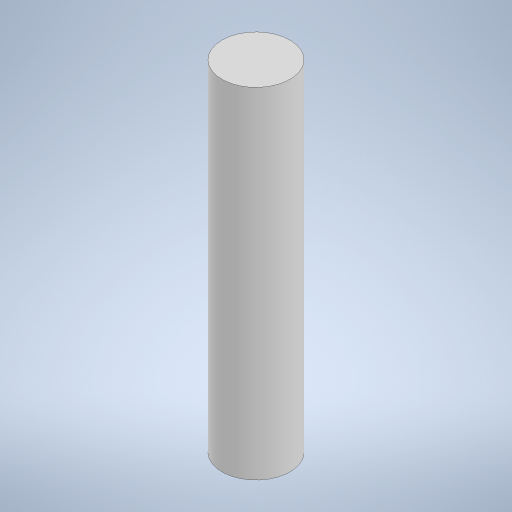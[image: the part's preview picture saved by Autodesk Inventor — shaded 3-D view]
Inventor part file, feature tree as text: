
AUTODESK INVENTOR PART (.ipt)
format: ipt  version: 2023 (Build 270158000, 158)  size: 215,040 bytes
history: native  units: mm
features: other x1, extrude x1, sketch x1
ambient origin geometry x8: Origin, YZ Plane, XZ Plane, XY Plane, X Axis, Y Axis, Z Axis, Center Point
bodies: Body1 (feature_tree)
feature tree (3):
  other  "솔리드1"
  extrude  "돌출1"  Depth=10.0mm
  sketch  "스케치1"
